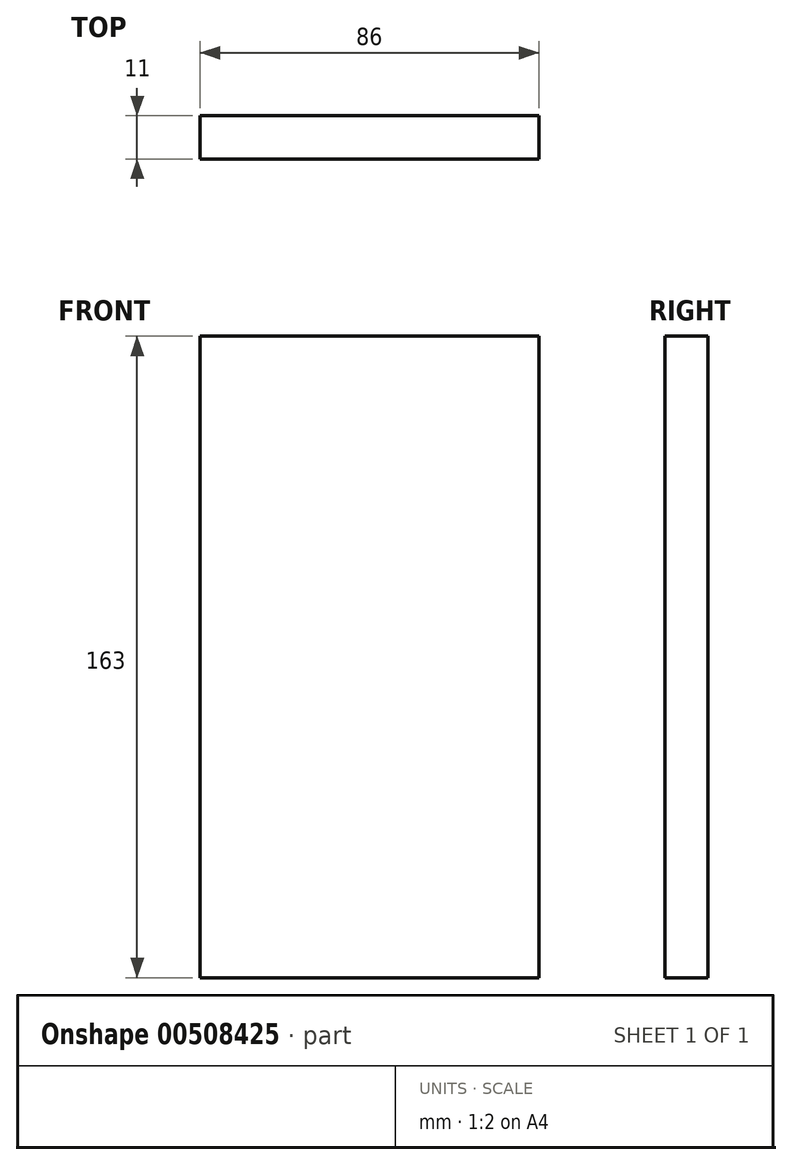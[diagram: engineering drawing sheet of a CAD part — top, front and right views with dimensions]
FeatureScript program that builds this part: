
annotation { "Feature Type Name" : "Feature", "Feature Type Description" : "" }
export const myFeature = defineFeature(function(context is Context, id is Id, definition is map)
    precondition{}
    {
        {
            var Q0;
            Q0=qCreatedBy(makeId("Front.planeOp"),FACE);
            var sketch = newSketch(context, id + "F0", { "sketchPlane" : qUnion([Q0])});
            skLineSegment(sketch, "E0.bottom", {"start": v(43, -81.5) * mm, "end": v(-43, -81.5) * mm});
            skLineSegment(sketch, "E0.top", {"start": v(43, 81.5) * mm, "end": v(-43, 81.5) * mm});
            skLineSegment(sketch, "E0.left", {"start": v(43, -81.5) * mm, "end": v(43, 81.5) * mm});
            skLineSegment(sketch, "E0.right", {"start": v(-43, -81.5) * mm, "end": v(-43, 81.5) * mm});
            skPoint(sketch, "E0.middle", {"position": v(0, 0) * mm});
            skSolve(sketch);
        }
        {
            var Q0;
            Q0=makeQuery(id+"F0.imprint","IMPRINT",FACE,{"disambiguationData":[TD([[makeQuery(id+"F0.imprint","IMPRINT",EDGE,{"derivedFrom":sQuery(id+"F0.wireOp",EDGE,"E0.bottom")}),-1.0]])]});
            extrude(context, id + "F1", {"entities" : qUnion([Q0]), "depth" : 11 * mm});
        }
    });
